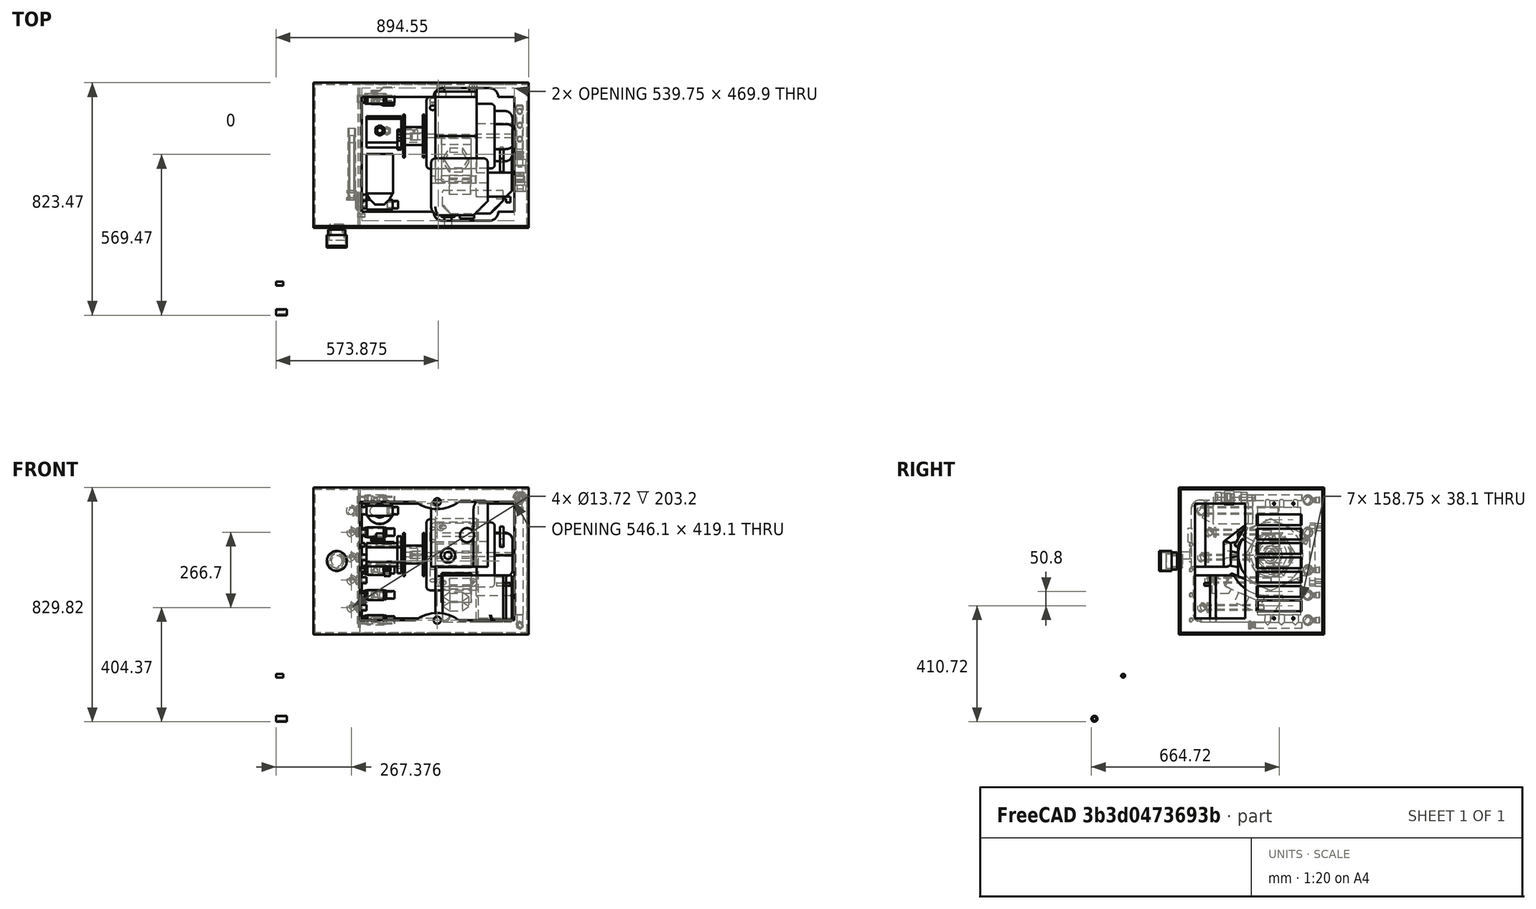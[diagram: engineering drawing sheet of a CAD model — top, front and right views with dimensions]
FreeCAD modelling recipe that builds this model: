
FCSTD DOCUMENT  (FreeCAD 0.16R6712 (Git))
Label: powercube v17.11
License: CreativeCommons Attribution-ShareAlike
LicenseURL: http://creativecommons.org/licenses/by-sa/4.0/
objects: App::FeaturePython×29, Part::FeaturePython×17, Part::Feature×9, App::DocumentObjectGroup×3
note: 26 computed .brp shape members not serialized (recipe doc carries the construction recipe); baked Part::Feature solids carry a one-line shape summary decoded from their .brp

FEATURE [Part::Feature] Cut002  label="0.75 NPT x 1.5in pipe section"
  Placement = pos=(-71.1581,-527.05,186.267) rot=(0,-1,0;1.5708rad)
  shape: bbox 38.1 x 26.67 x 26.67 mm, 4 faces (baked)
FEATURE [Part::Feature] Pad005  label="1/4" NPT pipe"
  Placement = pos=(-152.4,-203.2,-152.4) rot=(0.57735,0.57735,0.57735;2.0944rad)
  shape: bbox 25.4 x 13.72 x 13.72 mm, 4 faces (baked)
FEATURE [Part::FeaturePython] Clone039  label="Clone of 0.75 NPT x 1.5in pipe section005"  # Draft clone (typed FeaturePython)
  Objects = -> [Cut002]
  Placement = pos=(229.07,450.85,44.45) rot=(0,1,0;1.5708rad)
  Scale = (1,1,1)
FEATURE [Part::FeaturePython] Clone040  label="Clone of 0.75 NPT x 1.5in pipe section006"  # Draft clone (typed FeaturePython)
  Objects = -> [Cut002]
  Placement = pos=(229.07,450.85,133.35) rot=(0,1,0;1.5708rad)
  Scale = (1,1,1)
FEATURE [Part::FeaturePython] Clone041  label="Clone of 0.75 NPT x 1.5in pipe section007"  # Draft clone (typed FeaturePython)
  Objects = -> [Cut002]
  Placement = pos=(229.07,450.85,222.25) rot=(0,1,0;1.5708rad)
  Scale = (1,1,1)
FEATURE [Part::FeaturePython] Clone042  label="Clone of 0.75 NPT x 1.5in pipe section008"  # Draft clone (typed FeaturePython)
  Objects = -> [Cut002]
  Placement = pos=(229.07,450.85,355.6) rot=(0,1,0;1.5708rad)
  Scale = (1,1,1)
FEATURE [Part::FeaturePython] Clone043  label="Clone of 0.75 NPT x 1.5in pipe section009"  # Draft clone (typed FeaturePython)
  Objects = -> [Cut002]
  Placement = pos=(229.07,450.85,469.9) rot=(0,1,0;1.5708rad)
  Scale = (1,1,1)
FEATURE [Part::Feature] Pad006  label="engine rubber feet"
  Placement = pos=(-254,-203.2,254) rot=(1,0,0;1.5708rad)
  shape: bbox 25.4 x 25.4 x 25.4 mm, 4 faces (baked)
FEATURE [Part::FeaturePython] PC_1708_oil_filter_002  # a2plus imported part (geometry in sourceFile) (typed FeaturePython)
  Placement = pos=(214.465,115.824,431.8) rot=(1,0,0;1.5708rad)
  fixedPosition = false
  sourceFile = <userpath>/Documents/Freecad docs/Power Cube/PC_1708_oil_filter.fcstd
  timeLastImport = 0
  updateColors = true
FEATURE [Part::FeaturePython] Clone053  label="Clone of 0.75 NPT x 1.5in pipe section010"  # Draft clone (typed FeaturePython)
  Objects = -> [Cut002]
  Placement = pos=(241.77,76.2,431.8) rot=(0,1,0;1.5708rad)
  Scale = (1,1,1)
FEATURE [App::FeaturePython] circularEdgeConstraint35  label="circularEdgeConstraint35__PC_1708_oil_filter_002"  # a2plus constraint (typed FeaturePython)
  Object1 = Clone053
  Object2 = PC_1708_oil_filter_002
  SubElement1 = Edge3
  SubElement2 = Edge17
  Type = circularEdge
  directionConstraint = 0
  lockRotation = false
  offset = -19.05
FEATURE [App::FeaturePython] circularEdgeConstraint35_mirror  label="circularEdgeConstraint35__Clone of 0.75 NPT x 1.5in pipe section010"  # a2plus constraint (typed FeaturePython)
  Object1 = Clone053
  Object2 = PC_1708_oil_filter_002
  SubElement1 = Edge3
  SubElement2 = Edge17
  Type = circularEdge
  directionConstraint = 0
  lockRotation = false
  offset = -19.05
FEATURE [Part::Feature] Fusion001001  label="1240_cooler_and_fittings001"
  Placement = pos=(637.3,546.25,-104.8) rot=(0.57735,-0.57735,-0.57735;2.0944rad)
  shape: bbox 48 x 306.6 x 489 mm, 154 faces, 3 solids (baked)
FEATURE [Part::Feature] Pad001  label="0.5in x 1.5in NPT"
  Placement = pos=(-152.4,-304.8,-304.8) rot=(0.57735,0.57735,0.57735;2.0944rad)
  shape: bbox 38.1 x 21.34 x 21.34 mm, 4 faces (baked)
FEATURE [Part::FeaturePython] PC_v17_11_Frame_simple_01  # a2plus imported part (geometry in sourceFile) (typed FeaturePython)
  fixedPosition = true
  sourceFile = <userpath>/Documents/Power Cube v17.11/PC v17.11 Frame simple.fcstd
  timeLastImport = 1.53306e+09
  updateColors = true
FEATURE [App::DocumentObjectGroup] Group  label="Frame"
  Group = -> [PC_v17_11_Frame_simple_01]
FEATURE [Part::FeaturePython] Clone  label="Clone of engine rubber feet"  # Draft clone (typed FeaturePython)
  Objects = -> [Pad006]
  Placement = pos=(431,501.65,177.8) rot=(1,0,0;1.5708rad)
  Scale = (1,1,1)
FEATURE [Part::FeaturePython] Clone070  label="Clone of engine rubber feet001"  # Draft clone (typed FeaturePython)
  Objects = -> [Pad006]
  Placement = pos=(545.3,501.65,177.8) rot=(1,0,0;1.5708rad)
  Scale = (1,1,1)
FEATURE [Part::FeaturePython] Clone071  label="Clone of engine rubber feet002"  # Draft clone (typed FeaturePython)
  Objects = -> [Pad006]
  Placement = pos=(545.3,501.65,374.65) rot=(1,0,0;1.5708rad)
  Scale = (1,1,1)
FEATURE [Part::FeaturePython] Clone072  label="Clone of engine rubber feet003"  # Draft clone (typed FeaturePython)
  Objects = -> [Pad006]
  Placement = pos=(431,501.65,374.65) rot=(1,0,0;1.5708rad)
  Scale = (1,1,1)
FEATURE [App::FeaturePython] circularEdgeConstraint01  label="circularEdgeConstraint01__PC_v17_11_Frame_simple_01"  # a2plus constraint (typed FeaturePython)
  Object1 = Clone
  Object2 = PC_v17_11_Frame_simple_01
  SubElement1 = Edge5
  SubElement2 = Edge252
  Type = circularEdge
  directionConstraint = 0
  lockRotation = false
  offset = 0
FEATURE [App::FeaturePython] circularEdgeConstraint01_mirror  label="circularEdgeConstraint01__Clone of engine rubber feet"  # a2plus constraint (typed FeaturePython)
  Object1 = Clone
  Object2 = PC_v17_11_Frame_simple_01
  SubElement1 = Edge5
  SubElement2 = Edge252
  Type = circularEdge
  directionConstraint = 0
  lockRotation = false
  offset = 0
FEATURE [App::FeaturePython] circularEdgeConstraint02  label="circularEdgeConstraint02__Clone of engine rubber feet001"  # a2plus constraint (typed FeaturePython)
  Object1 = PC_v17_11_Frame_simple_01
  Object2 = Clone070
  SubElement1 = Edge249
  SubElement2 = Edge5
  Type = circularEdge
  directionConstraint = 0
  lockRotation = false
  offset = 0
FEATURE [App::FeaturePython] circularEdgeConstraint02_mirror  label="circularEdgeConstraint02__PC_v17_11_Frame_simple_01"  # a2plus constraint (typed FeaturePython)
  Object1 = PC_v17_11_Frame_simple_01
  Object2 = Clone070
  SubElement1 = Edge249
  SubElement2 = Edge5
  Type = circularEdge
  directionConstraint = 0
  lockRotation = false
  offset = 0
FEATURE [App::FeaturePython] circularEdgeConstraint03  label="circularEdgeConstraint03__PC_v17_11_Frame_simple_01"  # a2plus constraint (typed FeaturePython)
  Object1 = Clone071
  Object2 = PC_v17_11_Frame_simple_01
  SubElement1 = Edge5
  SubElement2 = Edge243
  Type = circularEdge
  directionConstraint = 0
  lockRotation = false
  offset = 0
FEATURE [App::FeaturePython] circularEdgeConstraint03_mirror  label="circularEdgeConstraint03__Clone of engine rubber feet002"  # a2plus constraint (typed FeaturePython)
  Object1 = Clone071
  Object2 = PC_v17_11_Frame_simple_01
  SubElement1 = Edge5
  SubElement2 = Edge243
  Type = circularEdge
  directionConstraint = 0
  lockRotation = false
  offset = 0
FEATURE [App::FeaturePython] circularEdgeConstraint04  label="circularEdgeConstraint04__Clone of engine rubber feet003"  # a2plus constraint (typed FeaturePython)
  Object1 = PC_v17_11_Frame_simple_01
  Object2 = Clone072
  SubElement1 = Edge246
  SubElement2 = Edge5
  Type = circularEdge
  directionConstraint = 0
  lockRotation = false
  offset = 0
FEATURE [App::FeaturePython] circularEdgeConstraint04_mirror  label="circularEdgeConstraint04__PC_v17_11_Frame_simple_01"  # a2plus constraint (typed FeaturePython)
  Object1 = PC_v17_11_Frame_simple_01
  Object2 = Clone072
  SubElement1 = Edge246
  SubElement2 = Edge5
  Type = circularEdge
  directionConstraint = 0
  lockRotation = false
  offset = 0
FEATURE [App::DocumentObjectGroup] Group001  label="Power"
  Group = -> [Pad006,Clone,Clone070,Clone071,Clone072,circularEdgeConstraint01,circularEdgeConstraint02_mirror,circularEdgeConstraint03,circularEdgeConstraint04_mirror]
FEATURE [App::FeaturePython] circularEdgeConstraint06_mirror  label="circularEdgeConstraint06__Clone of 1/4" NPT pipe"  # a2plus constraint (typed FeaturePython)
  Object1 = Clone073
  Object2 = PC_v17_11_Frame_simple_01
  SubElement1 = Edge6
  SubElement2 = Edge81
  Type = circularEdge
  directionConstraint = 1
  lockRotation = false
  offset = 0
FEATURE [App::DocumentObjectGroup] Group002  label="Plumbing"
  Group = -> [Pad001,Fusion001001,Cut002,Pad005,Clone039,Clone040,Clone041,Clone042,Clone043,PC_1708_oil_filter_002,Clone053,circularEdgeConstraint35,circularEdgeConstraint06_mirror]
FEATURE [Part::Feature] Compound002001  label="0.75in NPT Ball Valve"
  Placement = pos=(812.8,-175.26,330.2) rot=(-0.57735,-0.57735,-0.57735;2.0944rad)
  shape: bbox 104 x 60.2 x 35.56 mm, 53 faces, 5 solids (baked)
FEATURE [Part::FeaturePython] Clone077  label="Clone of 0.75in NPT Ball Valve"  # Draft clone (typed FeaturePython)
  Objects = -> [Compound002001]
  Placement = pos=(237.96,440.69,44.45) rot=(0.57735,0.57735,0.57735;4.18879rad)
  Scale = (1,1,1)
FEATURE [Part::FeaturePython] Clone078  label="Clone of 0.75in NPT Ball Valve001"  # Draft clone (typed FeaturePython)
  Objects = -> [Compound002001]
  Placement = pos=(237.96,440.69,133.35) rot=(0.57735,0.57735,0.57735;4.18879rad)
  Scale = (1,1,1)
FEATURE [Part::FeaturePython] Clone079  label="Clone of 0.75in NPT Ball Valve002"  # Draft clone (typed FeaturePython)
  Objects = -> [Compound002001]
  Placement = pos=(237.96,440.69,222.25) rot=(0.57735,0.57735,0.57735;4.18879rad)
  Scale = (1,1,1)
FEATURE [Part::FeaturePython] Clone080  label="Clone of 0.75in NPT Ball Valve003"  # Draft clone (typed FeaturePython)
  Objects = -> [Compound002001]
  Placement = pos=(237.96,454.305,365.155) rot=(0.701739,0.701739,-0.122979;2.89686rad)
  Scale = (1,1,1)
FEATURE [Part::FeaturePython] Clone081  label="Clone of 0.75in NPT Ball Valve004"  # Draft clone (typed FeaturePython)
  Objects = -> [Compound002001]
  Placement = pos=(237.96,440.69,469.9) rot=(0.57735,0.57735,0.57735;4.18879rad)
  Scale = (1,1,1)
FEATURE [App::FeaturePython] circularEdgeConstraint26  # a2plus constraint (typed FeaturePython)
  Object1 = Clone039
  Object2 = Clone077
  SubElement1 = Edge3
  SubElement2 = Edge59
  Type = circularEdge
  directionConstraint = 0
  lockRotation = false
  offset = -8.89
FEATURE [App::FeaturePython] circularEdgeConstraint27  # a2plus constraint (typed FeaturePython)
  Object1 = Clone040
  Object2 = Clone078
  SubElement1 = Edge3
  SubElement2 = Edge59
  Type = circularEdge
  directionConstraint = 0
  lockRotation = false
  offset = -8.89
FEATURE [App::FeaturePython] circularEdgeConstraint28  # a2plus constraint (typed FeaturePython)
  Object1 = Clone041
  Object2 = Clone079
  SubElement1 = Edge3
  SubElement2 = Edge59
  Type = circularEdge
  directionConstraint = 0
  lockRotation = false
  offset = -8.89
FEATURE [App::FeaturePython] circularEdgeConstraint30  # a2plus constraint (typed FeaturePython)
  Object1 = Clone043
  Object2 = Clone081
  SubElement1 = Edge3
  SubElement2 = Edge59
  Type = circularEdge
  directionConstraint = 0
  lockRotation = false
  offset = -8.89
FEATURE [Part::Feature] Compound002002002005003  label="engine_pump_module"
  Placement = pos=(297.65,744.033,-100.328) rot=(0,0,1;0rad)
  shape: bbox 517.5 x 482.5 x 432.2 mm, 345 faces, 25 solids (baked)
FEATURE [App::FeaturePython] circularEdgeConstraint05  label="cEc05_engine_module_vertical"  # a2plus constraint (typed FeaturePython)
  Object1 = Compound002002002005003
  Object2 = Clone071
  SubElement1 = Edge773
  SubElement2 = Edge6
  Type = circularEdge
  directionConstraint = 1
  lockRotation = false
  offset = 0
FEATURE [App::FeaturePython] circularEdgeConstraint06  label="circularEdgeConstraint06__PC_v17_11_Frame_simple_01"  # a2plus constraint (typed FeaturePython)
  Object1 = Clone081
  Object2 = PC_v17_11_Frame_simple_01
  SubElement1 = Edge72
  SubElement2 = Edge91
  Type = circularEdge
  directionConstraint = 0
  lockRotation = false
  offset = -12.7
FEATURE [App::FeaturePython] circularEdgeConstraint06_mirror001  label="circularEdgeConstraint06__Clone of 0.75in NPT Ball Valve004"  # a2plus constraint (typed FeaturePython)
  Object1 = Clone081
  Object2 = PC_v17_11_Frame_simple_01
  SubElement1 = Edge72
  SubElement2 = Edge91
  Type = circularEdge
  directionConstraint = 0
  lockRotation = false
  offset = -12.7
FEATURE [App::FeaturePython] circularEdgeConstraint07  label="circularEdgeConstraint07__PC_v17_11_Frame_simple_01"  # a2plus constraint (typed FeaturePython)
  Object1 = Clone077
  Object2 = PC_v17_11_Frame_simple_01
  SubElement1 = Edge72
  SubElement2 = Edge31
  Type = circularEdge
  directionConstraint = 0
  lockRotation = false
  offset = -12.7
FEATURE [App::FeaturePython] circularEdgeConstraint07_mirror  label="circularEdgeConstraint07__Clone of 0.75in NPT Ball Valve"  # a2plus constraint (typed FeaturePython)
  Object1 = Clone077
  Object2 = PC_v17_11_Frame_simple_01
  SubElement1 = Edge72
  SubElement2 = Edge31
  Type = circularEdge
  directionConstraint = 0
  lockRotation = false
  offset = -12.7
FEATURE [App::FeaturePython] circularEdgeConstraint08  label="circularEdgeConstraint08__PC_v17_11_Frame_simple_01"  # a2plus constraint (typed FeaturePython)
  Object1 = Clone078
  Object2 = PC_v17_11_Frame_simple_01
  SubElement1 = Edge72
  SubElement2 = Edge73
  Type = circularEdge
  directionConstraint = 0
  lockRotation = false
  offset = -12.7
FEATURE [App::FeaturePython] circularEdgeConstraint08_mirror  label="circularEdgeConstraint08__Clone of 0.75in NPT Ball Valve001"  # a2plus constraint (typed FeaturePython)
  Object1 = Clone078
  Object2 = PC_v17_11_Frame_simple_01
  SubElement1 = Edge72
  SubElement2 = Edge73
  Type = circularEdge
  directionConstraint = 0
  lockRotation = false
  offset = -12.7
FEATURE [App::FeaturePython] circularEdgeConstraint09  label="circularEdgeConstraint09__PC_v17_11_Frame_simple_01"  # a2plus constraint (typed FeaturePython)
  Object1 = Clone079
  Object2 = PC_v17_11_Frame_simple_01
  SubElement1 = Edge72
  SubElement2 = Edge79
  Type = circularEdge
  directionConstraint = 0
  lockRotation = false
  offset = -12.7
FEATURE [App::FeaturePython] circularEdgeConstraint09_mirror  label="circularEdgeConstraint09__Clone of 0.75in NPT Ball Valve002"  # a2plus constraint (typed FeaturePython)
  Object1 = Clone079
  Object2 = PC_v17_11_Frame_simple_01
  SubElement1 = Edge72
  SubElement2 = Edge79
  Type = circularEdge
  directionConstraint = 0
  lockRotation = false
  offset = -12.7
FEATURE [App::FeaturePython] circularEdgeConstraint10  label="circularEdgeConstraint10__PC_v17_11_Frame_simple_01"  # a2plus constraint (typed FeaturePython)
  Object1 = Clone080
  Object2 = PC_v17_11_Frame_simple_01
  SubElement1 = Edge72
  SubElement2 = Edge85
  Type = circularEdge
  directionConstraint = 0
  lockRotation = false
  offset = -12.7
FEATURE [App::FeaturePython] circularEdgeConstraint10_mirror  label="circularEdgeConstraint10__Clone of 0.75in NPT Ball Valve003"  # a2plus constraint (typed FeaturePython)
  Object1 = Clone080
  Object2 = PC_v17_11_Frame_simple_01
  SubElement1 = Edge72
  SubElement2 = Edge85
  Type = circularEdge
  directionConstraint = 0
  lockRotation = false
  offset = -12.7
FEATURE [App::FeaturePython] circularEdgeConstraint11  label="circularEdgeConstraint11_valve_out_"  # a2plus constraint (typed FeaturePython)
  Object1 = Clone042
  Object2 = Clone080
  SubElement1 = Edge3
  SubElement2 = Edge59
  Type = circularEdge
  directionConstraint = 0
  lockRotation = false
  offset = -8.89
FEATURE [Part::Feature] Compound001  label="SAE -12 to 3/4" adapter"
  Placement = pos=(163.889,288.901,412.982) rot=(0,0.999967,-0.008118;1.5708rad)
  shape: bbox 31.9 x 36.73 x 47.21 mm, 17 faces, 3 solids (baked)
FEATURE [App::FeaturePython] circularEdgeConstraint12  # a2plus constraint (typed FeaturePython)
  Object1 = Compound001
  Object2 = Compound002002002005003
  SubElement1 = Edge30
  SubElement2 = Edge88
  Type = circularEdge
  directionConstraint = 1
  lockRotation = false
  offset = 0
FEATURE [Part::Feature] Compound002002002005004  label="SAE 10 x 0.5in NPT"
  Placement = pos=(291.711,286.684,139.941) rot=(0,-0.999967,0.008118;1.5708rad)
  shape: bbox 25.52 x 29.4 x 47.17 mm, 17 faces, 3 solids (baked)
FEATURE [App::FeaturePython] circularEdgeConstraint13  # a2plus constraint (typed FeaturePython)
  Object1 = Compound002002002005004
  Object2 = Compound002002002005003
  SubElement1 = Edge30
  SubElement2 = Edge93
  Type = circularEdge
  directionConstraint = 1
  lockRotation = false
  offset = 0
